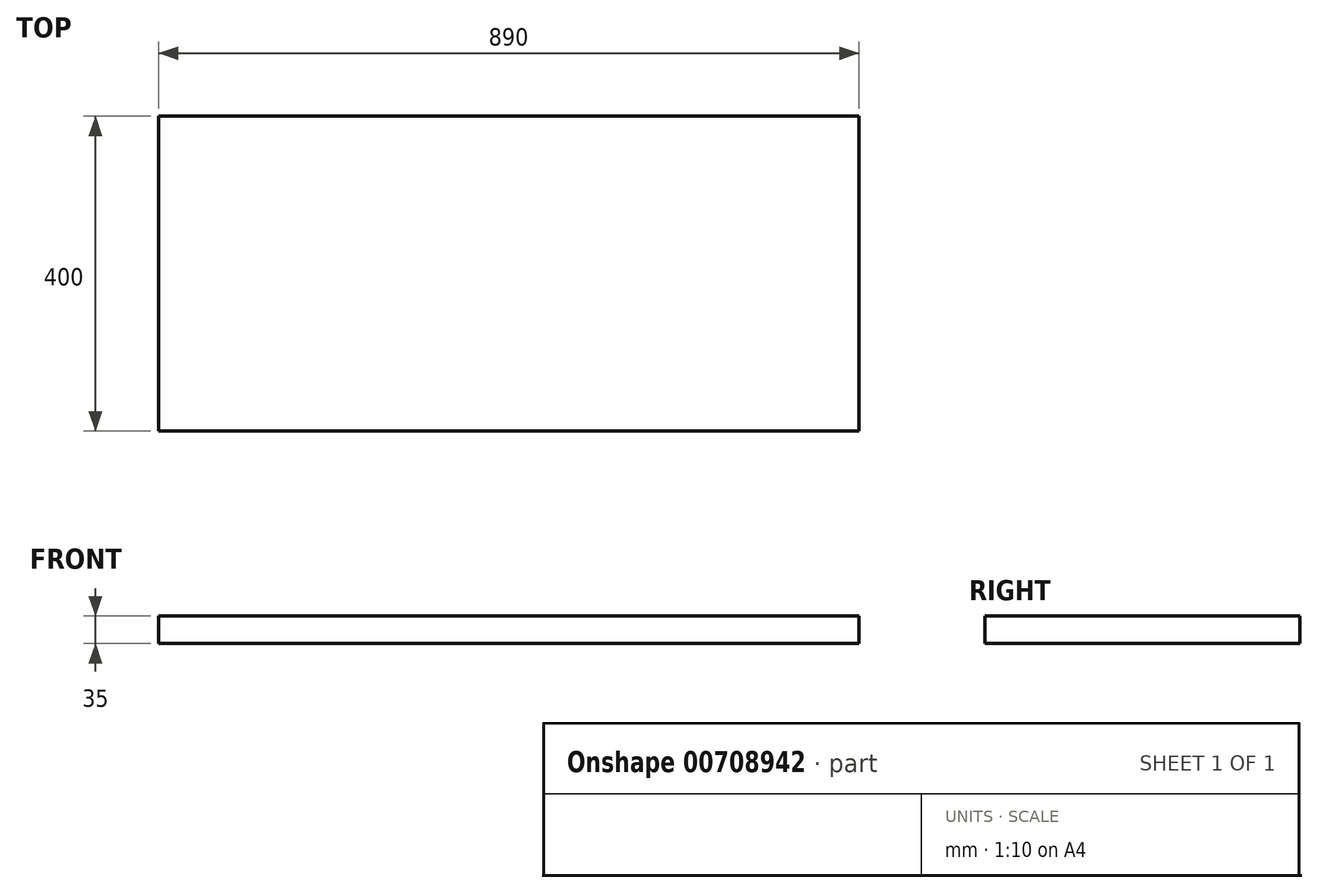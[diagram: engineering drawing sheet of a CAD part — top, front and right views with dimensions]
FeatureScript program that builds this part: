
annotation { "Feature Type Name" : "Feature", "Feature Type Description" : "" }
export const myFeature = defineFeature(function(context is Context, id is Id, definition is map)
    precondition{}
    {
        {
            var Q0;
            Q0=qCreatedBy(makeId("Top.planeOp"),FACE);
            var sketch = newSketch(context, id + "F0", { "sketchPlane" : qUnion([Q0])});
            skLineSegment(sketch, "E0.bottom", {"start": v(0, 0) * mm, "end": v(890, 0) * mm});
            skLineSegment(sketch, "E0.top", {"start": v(0, 400) * mm, "end": v(890, 400) * mm});
            skLineSegment(sketch, "E0.left", {"start": v(0, 0) * mm, "end": v(0, 400) * mm});
            skLineSegment(sketch, "E0.right", {"start": v(890, 0) * mm, "end": v(890, 400) * mm});
            skSolve(sketch);
        }
        {
            var Q0;
            Q0=makeQuery(id+"F0.imprint","IMPRINT",FACE,{"disambiguationData":[TD([[makeQuery(id+"F0.imprint","IMPRINT",EDGE,{"derivedFrom":sQuery(id+"F0.wireOp",EDGE,"E0.bottom")}),1.0]])]});
            extrude(context, id + "F1", {"entities" : qUnion([Q0]), "depth" : 35 * mm, "offsetDistance" : 25 * mm});
        }
    });
